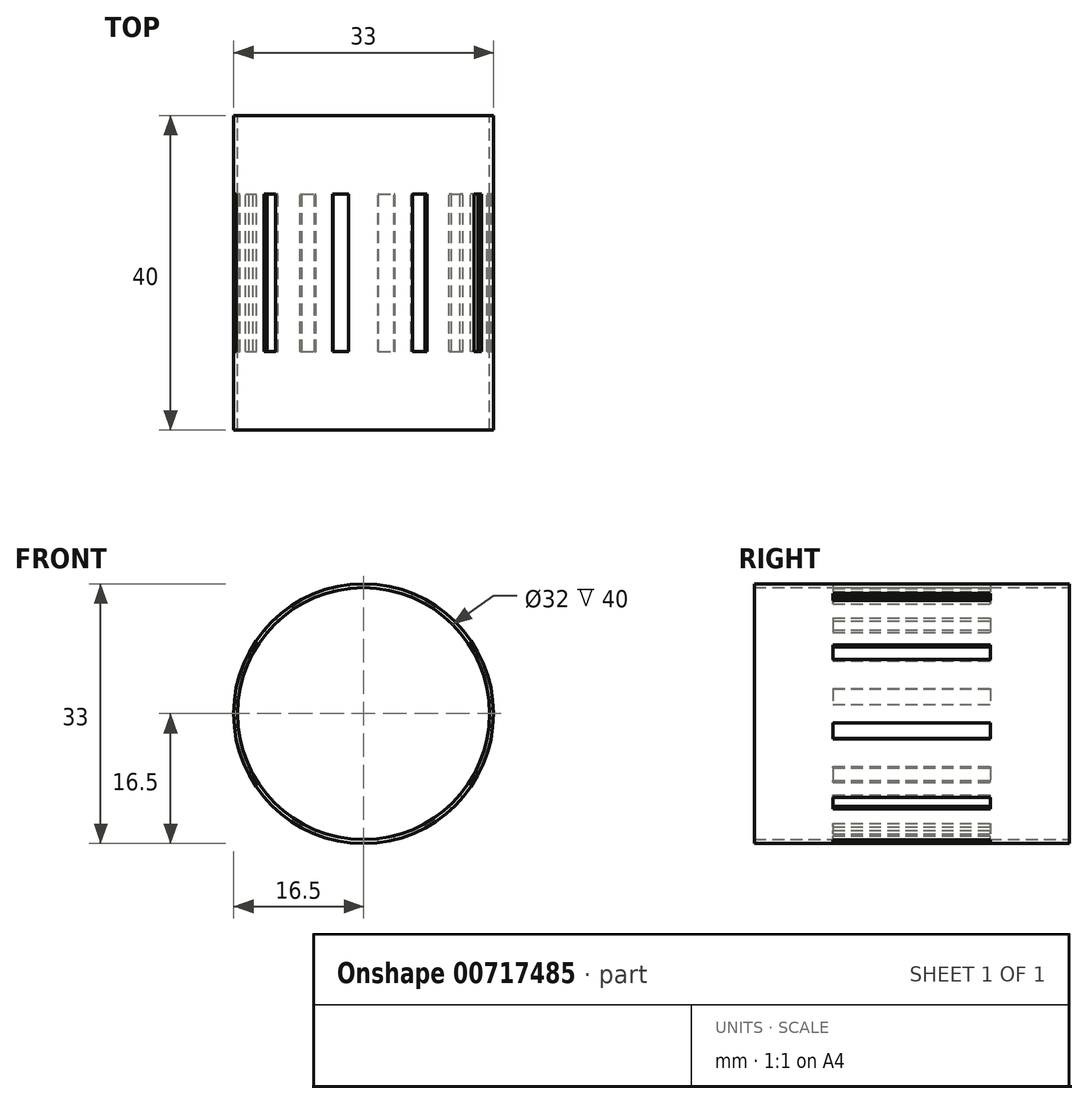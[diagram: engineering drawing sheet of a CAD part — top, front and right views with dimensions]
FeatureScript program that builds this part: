
annotation { "Feature Type Name" : "Feature", "Feature Type Description" : "" }
export const myFeature = defineFeature(function(context is Context, id is Id, definition is map)
    precondition{}
    {
        {
            var Q0;
            Q0=qCreatedBy(makeId("Front.planeOp"),FACE);
            var sketch = newSketch(context, id + "F0", { "sketchPlane" : qUnion([Q0])});
            skArc(sketch, "E0", {"start": v(-12.24, 10.3) * mm, "mid": v(-14.42, 6.94) * mm, "end": v(-15.69, 3.13) * mm});
            skLineSegment(sketch, "E1", {"start": v(6.2, 15.29) * mm, "end": v(6.02, 14.82) * mm});
            skLineSegment(sketch, "E2", {"start": v(8.07, 14.39) * mm, "end": v(7.83, 13.95) * mm});
            skLineSegment(sketch, "E3", {"start": v(14, 8.72) * mm, "end": v(13.58, 8.46) * mm});
            skLineSegment(sketch, "E4", {"start": v(15, 6.9) * mm, "end": v(14.54, 6.69) * mm});
            skLineSegment(sketch, "E5", {"start": v(16.46, -1.18) * mm, "end": v(15.96, -1.14) * mm});
            skLineSegment(sketch, "E6", {"start": v(16.18, -3.23) * mm, "end": v(15.7, -3.13) * mm});
            skLineSegment(sketch, "E7", {"start": v(12.62, -10.62) * mm, "end": v(12.24, -10.3) * mm});
            skLineSegment(sketch, "E8", {"start": v(11.2, -12.12) * mm, "end": v(10.85, -11.76) * mm});
            skLineSegment(sketch, "E9", {"start": v(-1.93, 16.39) * mm, "end": v(-1.87, 15.9) * mm});
            skLineSegment(sketch, "E10", {"start": v(-3.96, 16.02) * mm, "end": v(-3.84, 15.53) * mm});
            skLineSegment(sketch, "E11", {"start": v(-11.2, 12.13) * mm, "end": v(-10.85, 11.76) * mm});
            skLineSegment(sketch, "E12", {"start": v(-12.62, 10.63) * mm, "end": v(-12.24, 10.3) * mm});
            skLineSegment(sketch, "E13", {"start": v(-16.18, 3.23) * mm, "end": v(-15.69, 3.13) * mm});
            skLineSegment(sketch, "E14", {"start": v(-16.46, 1.18) * mm, "end": v(-15.96, 1.14) * mm});
            skLineSegment(sketch, "E15", {"start": v(-14.99, -6.9) * mm, "end": v(-14.53, -6.69) * mm});
            skLineSegment(sketch, "E16", {"start": v(-14, -8.72) * mm, "end": v(-13.58, -8.46) * mm});
            skLineSegment(sketch, "E17", {"start": v(-8.07, -14.4) * mm, "end": v(-7.83, -13.96) * mm});
            skLineSegment(sketch, "E18", {"start": v(-6.2, -15.29) * mm, "end": v(-6.02, -14.83) * mm});
            skLineSegment(sketch, "E19", {"start": v(1.93, -16.39) * mm, "end": v(1.87, -15.9) * mm});
            skLineSegment(sketch, "E20", {"start": v(3.97, -16.02) * mm, "end": v(3.85, -15.53) * mm});
            skArc(sketch, "E21.trimOffspring", {"start": v(-3.84, 15.53) * mm, "mid": v(-7.59, 14.09) * mm, "end": v(-10.85, 11.76) * mm});
            skArc(sketch, "E22.trimOffspring", {"start": v(3.85, -15.53) * mm, "mid": v(7.59, -14.09) * mm, "end": v(10.85, -11.76) * mm});
            skArc(sketch, "E23.trimOffspring", {"start": v(12.24, -10.3) * mm, "mid": v(14.42, -6.94) * mm, "end": v(15.7, -3.13) * mm});
            skArc(sketch, "E24.trimOffspring", {"start": v(15.96, -1.14) * mm, "mid": v(15.74, 2.86) * mm, "end": v(14.54, 6.69) * mm});
            skArc(sketch, "E25.trimOffspring", {"start": v(13.58, 8.46) * mm, "mid": v(11.05, 11.57) * mm, "end": v(7.83, 13.95) * mm});
            skArc(sketch, "E26.trimOffspring", {"start": v(6.02, 14.82) * mm, "mid": v(2.14, 15.86) * mm, "end": v(-1.87, 15.9) * mm});
            skArc(sketch, "E27.trimOffspring", {"start": v(-15.96, 1.14) * mm, "mid": v(-15.74, -2.86) * mm, "end": v(-14.53, -6.69) * mm});
            skArc(sketch, "E28.trimOffspring", {"start": v(-13.58, -8.46) * mm, "mid": v(-11.05, -11.57) * mm, "end": v(-7.83, -13.96) * mm});
            skArc(sketch, "E29.trimOffspring", {"start": v(-6.02, -14.83) * mm, "mid": v(-2.14, -15.86) * mm, "end": v(1.87, -15.9) * mm});
            skArc(sketch, "E30", {"start": v(-6.2, -15.29) * mm, "mid": v(-2.2, -16.35) * mm, "end": v(1.93, -16.39) * mm});
            skArc(sketch, "E31.trimOffspring", {"start": v(-14, -8.72) * mm, "mid": v(-11.4, -11.93) * mm, "end": v(-8.07, -14.4) * mm});
            skArc(sketch, "E32.trimOffspring", {"start": v(-16.46, 1.18) * mm, "mid": v(-16.23, -2.95) * mm, "end": v(-14.99, -6.9) * mm});
            skArc(sketch, "E33.trimOffspring", {"start": v(-12.62, 10.63) * mm, "mid": v(-14.87, 7.15) * mm, "end": v(-16.18, 3.23) * mm});
            skArc(sketch, "E34.trimOffspring", {"start": v(-3.96, 16.02) * mm, "mid": v(-7.82, 14.53) * mm, "end": v(-11.2, 12.13) * mm});
            skArc(sketch, "E35.trimOffspring", {"start": v(6.2, 15.29) * mm, "mid": v(2.21, 16.35) * mm, "end": v(-1.93, 16.39) * mm});
            skArc(sketch, "E36.trimOffspring", {"start": v(3.97, -16.02) * mm, "mid": v(7.83, -14.53) * mm, "end": v(11.2, -12.12) * mm});
            skArc(sketch, "E37.trimOffspring", {"start": v(12.62, -10.62) * mm, "mid": v(14.87, -7.15) * mm, "end": v(16.18, -3.23) * mm});
            skArc(sketch, "E38.trimOffspring", {"start": v(16.46, -1.18) * mm, "mid": v(16.23, 2.95) * mm, "end": v(15, 6.9) * mm});
            skArc(sketch, "E39.trimOffspring", {"start": v(14, 8.72) * mm, "mid": v(11.4, 11.93) * mm, "end": v(8.07, 14.39) * mm});
            skSolve(sketch);
        }
        {
            var Q0;
            Q0=makeQuery(id+"F0.imprint","IMPRINT",FACE,{"disambiguationData":[TD([[makeQuery(id+"F0.imprint","IMPRINT",EDGE,{"derivedFrom":sQuery(id+"F0.wireOp",EDGE,"E10")}),-1.0]])]});
            var Q1;
            Q1=makeQuery(id+"F0.imprint","IMPRINT",FACE,{"disambiguationData":[TD([[makeQuery(id+"F0.imprint","IMPRINT",EDGE,{"derivedFrom":sQuery(id+"F0.wireOp",EDGE,"E0")}),-1.0]])]});
            var Q2;
            Q2=makeQuery(id+"F0.imprint","IMPRINT",FACE,{"disambiguationData":[TD([[makeQuery(id+"F0.imprint","IMPRINT",EDGE,{"derivedFrom":sQuery(id+"F0.wireOp",EDGE,"E14")}),-1.0]])]});
            var Q3;
            Q3=makeQuery(id+"F0.imprint","IMPRINT",FACE,{"disambiguationData":[TD([[makeQuery(id+"F0.imprint","IMPRINT",EDGE,{"derivedFrom":sQuery(id+"F0.wireOp",EDGE,"E16")}),-1.0]])]});
            var Q4;
            Q4=makeQuery(id+"F0.imprint","IMPRINT",FACE,{"disambiguationData":[TD([[makeQuery(id+"F0.imprint","IMPRINT",EDGE,{"derivedFrom":sQuery(id+"F0.wireOp",EDGE,"E18")}),-1.0]])]});
            var Q5;
            Q5=makeQuery(id+"F0.imprint","IMPRINT",FACE,{"disambiguationData":[TD([[makeQuery(id+"F0.imprint","IMPRINT",EDGE,{"derivedFrom":sQuery(id+"F0.wireOp",EDGE,"E1")}),-1.0]])]});
            var Q6;
            Q6=makeQuery(id+"F0.imprint","IMPRINT",FACE,{"disambiguationData":[TD([[makeQuery(id+"F0.imprint","IMPRINT",EDGE,{"derivedFrom":sQuery(id+"F0.wireOp",EDGE,"E2")}),1.0]])]});
            var Q7;
            Q7=makeQuery(id+"F0.imprint","IMPRINT",FACE,{"disambiguationData":[TD([[makeQuery(id+"F0.imprint","IMPRINT",EDGE,{"derivedFrom":sQuery(id+"F0.wireOp",EDGE,"E4")}),1.0]])]});
            var Q8;
            Q8=makeQuery(id+"F0.imprint","IMPRINT",FACE,{"disambiguationData":[TD([[makeQuery(id+"F0.imprint","IMPRINT",EDGE,{"derivedFrom":sQuery(id+"F0.wireOp",EDGE,"E8")}),1.0]])]});
            var Q9;
            Q9=makeQuery(id+"F0.imprint","IMPRINT",FACE,{"disambiguationData":[TD([[makeQuery(id+"F0.imprint","IMPRINT",EDGE,{"derivedFrom":sQuery(id+"F0.wireOp",EDGE,"E6")}),1.0]])]});
            extrude(context, id + "F1", {"entities" : qUnion([Q0, Q1, Q2, Q3, Q4, Q5, Q6, Q7, Q8, Q9]), "depth" : 20 * mm, "offsetDistance" : 25 * mm});
        }
        {
            var Q0;
            Q0=makeQuery(id+"F0.imprint","IMPRINT",FACE,{"disambiguationData":[TD([[makeQuery(id+"F0.imprint","IMPRINT",EDGE,{"derivedFrom":sQuery(id+"F0.wireOp",EDGE,"E0")}),-1.0]])]});
            var sketch = newSketch(context, id + "F2", { "sketchPlane" : qUnion([Q0])});
            skCircle(sketch, "E40", {"center": v(0, 0) * mm, "radius": 16 * mm});
            skCircle(sketch, "E41", {"center": v(0, 0) * mm, "radius": 16.5 * mm});
            skSolve(sketch);
        }
        {
            var Q0;
            Q0 = qSketchRegion(id + "F2", true);
            extrude(context, id + "F3", {"entities" : qUnion([Q0]), "operationType" : NewBodyOperationType.ADD, "oppositeDirection" : true, "depth" : 10 * mm, "offsetDistance" : 25 * mm});
        }
        {
            var Q0;
            Q0=makeQuery(id+"F1.opExtrude","CAP_FACE",FACE,{"disambiguationData":[OSD([sQuery(id+"F0.wireOp",EDGE,"E0"),sQuery(id+"F0.wireOp",EDGE,"E12"),sQuery(id+"F0.wireOp",EDGE,"E13"),sQuery(id+"F0.wireOp",EDGE,"E33.trimOffspring")])],"isStart":false});
            var sketch = newSketch(context, id + "F4", { "sketchPlane" : qUnion([Q0])});
            skCircle(sketch, "E42", {"center": v(0, 0) * mm, "radius": 16 * mm});
            skCircle(sketch, "E43", {"center": v(0, 0) * mm, "radius": 16.5 * mm});
            skSolve(sketch);
        }
        {
            var Q0;
            Q0 = qSketchRegion(id + "F4", true);
            extrude(context, id + "F5", {"entities" : qUnion([Q0]), "operationType" : NewBodyOperationType.ADD, "depth" : 10 * mm, "offsetDistance" : 25 * mm});
        }
    });
